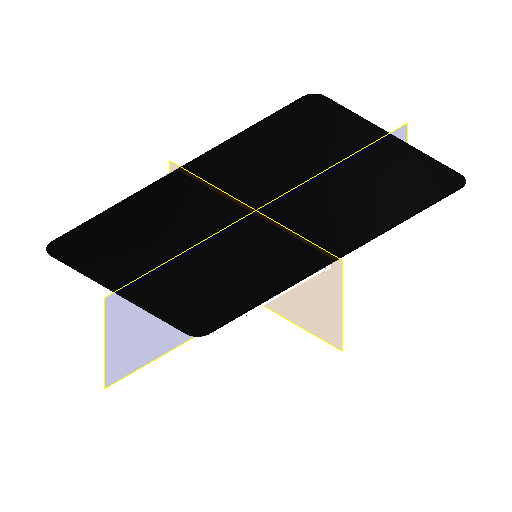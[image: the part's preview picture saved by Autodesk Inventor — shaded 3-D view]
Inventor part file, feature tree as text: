
AUTODESK INVENTOR PART (.ipt)
format: ipt  version: 2025.1 (Build 291241020, 241B)  size: 7,592,448 bytes
history: native  units: mm
features: other x246, plane x2
ambient origin geometry x8: Origin, YZ Plane, XZ Plane, XY Plane, X Axis, Y Axis, Z Axis, Center Point
bodies: Volumenkörper1 (feature_tree), Volumenkörper2 (feature_tree), Volumenkörper3 (feature_tree), Volumenkörper4 (feature_tree), Volumenkörper5 (feature_tree), Volumenkörper6 (feature_tree), Volumenkörper7 (feature_tree), Volumenkörper8 (feature_tree), Volumenkörper9 (feature_tree), Volumenkörper10 (feature_tree), Volumenkörper11 (feature_tree), Volumenkörper12 (feature_tree), Volumenkörper13 (feature_tree), Volumenkörper14 (feature_tree), Volumenkörper15 (feature_tree), Volumenkörper16 (feature_tree), Volumenkörper17 (feature_tree), Volumenkörper18 (feature_tree), Volumenkörper19 (feature_tree), Volumenkörper20 (feature_tree), Volumenkörper21 (feature_tree), Volumenkörper22 (feature_tree), Volumenkörper23 (feature_tree), Volumenkörper24 (feature_tree), Volumenkörper25 (feature_tree), Volumenkörper26 (feature_tree), Volumenkörper27 (feature_tree), Volumenkörper28 (feature_tree), Volumenkörper29 (feature_tree), Volumenkörper30 (feature_tree), Volumenkörper31 (feature_tree), Volumenkörper32 (feature_tree), Volumenkörper33 (feature_tree), Volumenkörper34 (feature_tree), Volumenkörper35 (feature_tree), Volumenkörper36 (feature_tree), Volumenkörper37 (feature_tree), Volumenkörper38 (feature_tree), Volumenkörper39 (feature_tree), Volumenkörper40 (feature_tree), Volumenkörper41 (feature_tree), Volumenkörper42 (feature_tree), Volumenkörper43 (feature_tree), Volumenkörper44 (feature_tree), Volumenkörper45 (feature_tree), Volumenkörper46 (feature_tree), Volumenkörper47 (feature_tree), Volumenkörper48 (feature_tree), Volumenkörper49 (feature_tree), Volumenkörper50 (feature_tree), Volumenkörper51 (feature_tree), Volumenkörper52 (feature_tree), Volumenkörper53 (feature_tree), Volumenkörper54 (feature_tree), Volumenkörper55 (feature_tree), Volumenkörper56 (feature_tree), Volumenkörper57 (feature_tree), Volumenkörper58 (feature_tree), Volumenkörper59 (feature_tree), Volumenkörper60 (feature_tree), Volumenkörper61 (feature_tree), Volumenkörper62 (feature_tree), Volumenkörper63 (feature_tree), Volumenkörper64 (feature_tree), Volumenkörper65 (feature_tree), Volumenkörper66 (feature_tree), Volumenkörper67 (feature_tree), Volumenkörper68 (feature_tree), Volumenkörper69 (feature_tree), Volumenkörper70 (feature_tree), Volumenkörper71 (feature_tree), Volumenkörper72 (feature_tree), Volumenkörper73 (feature_tree), Volumenkörper74 (feature_tree), Volumenkörper75 (feature_tree), Volumenkörper76 (feature_tree), Volumenkörper77 (feature_tree), Volumenkörper78 (feature_tree), Volumenkörper79 (feature_tree), Volumenkörper80 (feature_tree), Volumenkörper81 (feature_tree), Volumenkörper82 (feature_tree), Volumenkörper83 (feature_tree), Volumenkörper84 (feature_tree), Volumenkörper85 (feature_tree), Volumenkörper86 (feature_tree), Volumenkörper87 (feature_tree), Volumenkörper88 (feature_tree), Volumenkörper89 (feature_tree), Volumenkörper90 (feature_tree), Volumenkörper91 (feature_tree), Volumenkörper92 (feature_tree), Volumenkörper93 (feature_tree), Volumenkörper94 (feature_tree), Volumenkörper95 (feature_tree), Volumenkörper96 (feature_tree), Volumenkörper97 (feature_tree), Volumenkörper98 (feature_tree), Volumenkörper99 (feature_tree), Volumenkörper100 (feature_tree), Volumenkörper101 (feature_tree), Volumenkörper102 (feature_tree), Volumenkörper103 (feature_tree), Volumenkörper104 (feature_tree), Volumenkörper105 (feature_tree), Volumenkörper106 (feature_tree), Volumenkörper107 (feature_tree), Volumenkörper108 (feature_tree), Volumenkörper109 (feature_tree), Volumenkörper110 (feature_tree), Volumenkörper111 (feature_tree), Volumenkörper112 (feature_tree), Volumenkörper113 (feature_tree), Volumenkörper114 (feature_tree), Volumenkörper115 (feature_tree), Volumenkörper116 (feature_tree), Volumenkörper117 (feature_tree), Volumenkörper118 (feature_tree), Volumenkörper119 (feature_tree), Volumenkörper120 (feature_tree), Volumenkörper121 (feature_tree), Volumenkörper122 (feature_tree), Volumenkörper123 (feature_tree), Volumenkörper124 (feature_tree), Volumenkörper125 (feature_tree), Volumenkörper126 (feature_tree), Volumenkörper127 (feature_tree), Volumenkörper128 (feature_tree), Volumenkörper129 (feature_tree), Volumenkörper130 (feature_tree), Volumenkörper131 (feature_tree), Volumenkörper132 (feature_tree), Volumenkörper133 (feature_tree), Volumenkörper134 (feature_tree), Volumenkörper135 (feature_tree), Volumenkörper136 (feature_tree), Volumenkörper137 (feature_tree), Volumenkörper138 (feature_tree), Volumenkörper139 (feature_tree), Volumenkörper140 (feature_tree), Volumenkörper141 (feature_tree), Volumenkörper142 (feature_tree), Volumenkörper143 (feature_tree), Volumenkörper144 (feature_tree), Volumenkörper145 (feature_tree), Volumenkörper146 (feature_tree), Volumenkörper147 (feature_tree), Volumenkörper148 (feature_tree), Volumenkörper149 (feature_tree), Volumenkörper150 (feature_tree), Volumenkörper151 (feature_tree), Volumenkörper152 (feature_tree), Volumenkörper153 (feature_tree), Volumenkörper154 (feature_tree), Volumenkörper155 (feature_tree), Volumenkörper156 (feature_tree), Volumenkörper157 (feature_tree), Volumenkörper158 (feature_tree), Volumenkörper159 (feature_tree), Volumenkörper160 (feature_tree), Volumenkörper161 (feature_tree), Volumenkörper162 (feature_tree), Volumenkörper163 (feature_tree), Volumenkörper164 (feature_tree), Volumenkörper165 (feature_tree), Volumenkörper166 (feature_tree), Volumenkörper167 (feature_tree), Volumenkörper168 (feature_tree), Volumenkörper169 (feature_tree), Volumenkörper170 (feature_tree), Volumenkörper171 (feature_tree), Volumenkörper172 (feature_tree), Volumenkörper173 (feature_tree), Volumenkörper174 (feature_tree), Volumenkörper175 (feature_tree), Volumenkörper176 (feature_tree), Volumenkörper177 (feature_tree), Volumenkörper178 (feature_tree), Volumenkörper179 (feature_tree), Volumenkörper180 (feature_tree), Volumenkörper181 (feature_tree), Volumenkörper182 (feature_tree), Volumenkörper183 (feature_tree), Volumenkörper184 (feature_tree), Volumenkörper185 (feature_tree), Volumenkörper186 (feature_tree), Volumenkörper187 (feature_tree), Volumenkörper188 (feature_tree), Volumenkörper189 (feature_tree), Volumenkörper190 (feature_tree), Volumenkörper191 (feature_tree), Volumenkörper192 (feature_tree), Volumenkörper193 (feature_tree), Volumenkörper194 (feature_tree), Volumenkörper195 (feature_tree), Volumenkörper196 (feature_tree), Volumenkörper197 (feature_tree), Volumenkörper198 (feature_tree), Volumenkörper199 (feature_tree), Volumenkörper200 (feature_tree), Volumenkörper201 (feature_tree), Volumenkörper202 (feature_tree), Volumenkörper203 (feature_tree), Volumenkörper204 (feature_tree), Volumenkörper205 (feature_tree), Volumenkörper206 (feature_tree), Volumenkörper207 (feature_tree), Volumenkörper208 (feature_tree), Volumenkörper209 (feature_tree), Volumenkörper210 (feature_tree), Volumenkörper211 (feature_tree), Volumenkörper212 (feature_tree), Volumenkörper213 (feature_tree), Volumenkörper214 (feature_tree), Volumenkörper215 (feature_tree), Volumenkörper216 (feature_tree), Volumenkörper217 (feature_tree), Volumenkörper218 (feature_tree), Volumenkörper219 (feature_tree), Volumenkörper220 (feature_tree), Volumenkörper221 (feature_tree), Volumenkörper222 (feature_tree), Volumenkörper223 (feature_tree), Volumenkörper224 (feature_tree), Volumenkörper225 (feature_tree), Volumenkörper226 (feature_tree), Volumenkörper227 (feature_tree), Volumenkörper228 (feature_tree), Volumenkörper229 (feature_tree), Volumenkörper230 (feature_tree), Volumenkörper231 (feature_tree), Volumenkörper232 (feature_tree), Volumenkörper233 (feature_tree), Volumenkörper234 (feature_tree), Volumenkörper235 (feature_tree), Volumenkörper236 (feature_tree), Volumenkörper237 (feature_tree), Volumenkörper238 (feature_tree), Volumenkörper239 (feature_tree), Volumenkörper240 (feature_tree), Volumenkörper241 (feature_tree), Volumenkörper242 (feature_tree), Volumenkörper243 (feature_tree), Volumenkörper244 (feature_tree), Volumenkörper245 (feature_tree), Volumenkörper246 (feature_tree)
feature tree (248):
  plane  "Arbeitsebene1"
  plane  "Arbeitsebene2"
  other  "raspberry pi display_1:1"
  other  "raspberry pi display_1:2"
  other  "raspberry pi display_1:3"
  other  "Raspberry Pi 3 _1:1"
  other  "Raspberry Pi 3 _1:2"
  other  "Raspberry Pi 3 _1:3"
  other  "Raspberry Pi 3 _1:4"
  other  "Raspberry Pi 3 _1:5"
  other  "Raspberry Pi 3 _1:6"
  other  "Raspberry Pi 3 _1:7"
  other  "Raspberry Pi 3 _1:8"
  other  "Raspberry Pi 3 _1:9"
  other  "Raspberry Pi 3 _1:10"
  other  "Raspberry Pi 3 _1:11"
  other  "Raspberry Pi 3 _1:12"
  other  "Raspberry Pi 3 _1:13"
  other  "Raspberry Pi 3 _1:14"
  other  "Raspberry Pi 3 _1:15"
  other  "Raspberry Pi 3 _1:16"
  other  "Raspberry Pi 3 _1:17"
  other  "Raspberry Pi 3 _1:18"
  other  "Raspberry Pi 3 _1:19"
  other  "Raspberry Pi 3 _1:20"
  other  "Raspberry Pi 3 _1:21"
  other  "Raspberry Pi 3 _1:22"
  other  "Raspberry Pi 3 _1:23"
  other  "Raspberry Pi 3 _1:24"
  other  "Raspberry Pi 3 _1:25"
  other  "Raspberry Pi 3 _1:26"
  other  "Raspberry Pi 3 _1:27"
  other  "Raspberry Pi 3 _1:28"
  other  "Raspberry Pi 3 _1:29"
  other  "Raspberry Pi 3 _1:30"
  other  "Raspberry Pi 3 _1:31"
  other  "Raspberry Pi 3 _1:32"
  other  "Raspberry Pi 3 _1:33"
  other  "Raspberry Pi 3 _1:34"
  other  "Raspberry Pi 3 _1:35"
  other  "Raspberry Pi 3 _1:36"
  other  "Raspberry Pi 3 _1:37"
  other  "Raspberry Pi 3 _1:38"
  other  "Raspberry Pi 3 _1:39"
  other  "Raspberry Pi 3 _1:40"
  other  "Raspberry Pi 3 _1:41"
  other  "Raspberry Pi 3 _1:42"
  other  "Raspberry Pi 3 _1:43"
  other  "Raspberry Pi 3 _1:44"
  other  "Raspberry Pi 3 _1:45"
  other  "Raspberry Pi 3 _1:46"
  other  "Raspberry Pi 3 _1:47"
  other  "Raspberry Pi 3 _1:48"
  other  "Raspberry Pi 3 _1:49"
  other  "Raspberry Pi 3 _1:50"
  other  "Raspberry Pi 3 _1:51"
  other  "Raspberry Pi 3 _1:52"
  other  "Raspberry Pi 3 _1:53"
  other  "Raspberry Pi 3 _1:54"
  other  "Raspberry Pi 3 _1:55"
  other  "Raspberry Pi 3 _1:56"
  other  "Raspberry Pi 3 _1:57"
  other  "Raspberry Pi 3 _1:58"
  other  "Raspberry Pi 3 _1:59"
  other  "Raspberry Pi 3 _1:60"
  other  "Raspberry Pi 3 _1:61"
  other  "Raspberry Pi 3 _1:62"
  other  "Raspberry Pi 3 _1:63"
  other  "Raspberry Pi 3 _1:64"
  other  "Raspberry Pi 3 _1:65"
  other  "Raspberry Pi 3 _1:66"
  other  "Raspberry Pi 3 _1:67"
  other  "Raspberry Pi 3 _1:68"
  other  "Raspberry Pi 3 _1:69"
  other  "Raspberry Pi 3 _1:70"
  other  "Raspberry Pi 3 _1:71"
  other  "Raspberry Pi 3 _1:72"
  other  "Raspberry Pi 3 _1:73"
  other  "Raspberry Pi 3 _1:74"
  other  "Raspberry Pi 3 _1:75"
  other  "Raspberry Pi 3 _1:76"
  other  "Raspberry Pi 3 _1:77"
  other  "Raspberry Pi 3 _1:78"
  other  "Raspberry Pi 3 _1:79"
  other  "Raspberry Pi 3 _1:80"
  other  "Raspberry Pi 3 _1:81"
  other  "Raspberry Pi 3 _1:82"
  other  "Raspberry Pi 3 _1:83"
  other  "Raspberry Pi 3 _1:84"
  other  "Raspberry Pi 3 _1:85"
  other  "Raspberry Pi 3 _1:86"
  other  "Raspberry Pi 3 _1:87"
  other  "Raspberry Pi 3 _1:88"
  other  "Raspberry Pi 3 _1:89"
  other  "Raspberry Pi 3 _1:90"
  other  "Raspberry Pi 3 _1:91"
  other  "Raspberry Pi 3 _1:92"
  other  "Raspberry Pi 3 _1:93"
  other  "Raspberry Pi 3 _1:94"
  other  "Raspberry Pi 3 _1:95"
  other  "Raspberry Pi 3 _1:96"
  other  "Raspberry Pi 3 _1:97"
  other  "Raspberry Pi 3 _1:98"
  other  "Raspberry Pi 3 _1:99"
  other  "Raspberry Pi 3 _1:100"
  other  "Raspberry Pi 3 _1:101"
  other  "Raspberry Pi 3 _1:102"
  other  "Raspberry Pi 3 _1:103"
  other  "Raspberry Pi 3 _1:104"
  other  "Raspberry Pi 3 _1:105"
  other  "Raspberry Pi 3 _1:106"
  other  "Raspberry Pi 3 _1:107"
  other  "Raspberry Pi 3 _1:108"
  other  "Raspberry Pi 3 _1:109"
  other  "Raspberry Pi 3 _1:110"
  other  "Raspberry Pi 3 _1:111"
  other  "Raspberry Pi 3 _1:112"
  other  "Raspberry Pi 3 _1:113"
  other  "Raspberry Pi 3 _1:114"
  other  "Raspberry Pi 3 _1:115"
  other  "Raspberry Pi 3 _1:116"
  other  "Raspberry Pi 3 _1:117"
  other  "Raspberry Pi 3 _1:118"
  other  "Raspberry Pi 3 _1:119"
  other  "Raspberry Pi 3 _1:120"
  other  "Raspberry Pi 3 _1:121"
  other  "Raspberry Pi 3 _1:122"
  other  "Raspberry Pi 3 _1:123"
  other  "Raspberry Pi 3 _1:124"
  other  "Raspberry Pi 3 _1:125"
  other  "Raspberry Pi 3 _1:126"
  other  "Raspberry Pi 3 _1:127"
  other  "Raspberry Pi 3 _1:128"
  other  "Raspberry Pi 3 _1:129"
  other  "Raspberry Pi 3 _1:130"
  other  "Raspberry Pi 3 _1:131"
  other  "Raspberry Pi 3 _1:132"
  other  "Raspberry Pi 3 _1:133"
  other  "Raspberry Pi 3 _1:134"
  other  "Raspberry Pi 3 _1:135"
  other  "Raspberry Pi 3 _1:136"
  other  "Raspberry Pi 3 _1:137"
  other  "Raspberry Pi 3 _1:138"
  other  "Raspberry Pi 3 _1:139"
  other  "Raspberry Pi 3 _1:140"
  other  "Raspberry Pi 3 _1:141"
  other  "Raspberry Pi 3 _1:142"
  other  "Raspberry Pi 3 _1:143"
  other  "Raspberry Pi 3 _1:144"
  other  "Raspberry Pi 3 _1:145"
  other  "Raspberry Pi 3 _1:146"
  other  "Raspberry Pi 3 _1:147"
  other  "Raspberry Pi 3 _1:148"
  other  "Raspberry Pi 3 _1:149"
  other  "Raspberry Pi 3 _1:150"
  other  "Raspberry Pi 3 _1:151"
  other  "Raspberry Pi 3 _1:152"
  other  "Raspberry Pi 3 _1:153"
  other  "Raspberry Pi 3 _1:154"
  other  "Raspberry Pi 3 _1:155"
  other  "Raspberry Pi 3 _1:156"
  other  "Raspberry Pi 3 _1:157"
  other  "Raspberry Pi 3 _1:158"
  other  "Raspberry Pi 3 _1:159"
  other  "Raspberry Pi 3 _1:160"
  other  "Raspberry Pi 3 _1:161"
  other  "Raspberry Pi 3 _1:162"
  other  "Raspberry Pi 3 _1:163"
  other  "Raspberry Pi 3 _1:164"
  other  "Raspberry Pi 3 _1:165"
  other  "Raspberry Pi 3 _1:166"
  other  "Raspberry Pi 3 _1:167"
  other  "Raspberry Pi 3 _1:168"
  other  "Raspberry Pi 3 _1:169"
  other  "Raspberry Pi 3 _1:170"
  other  "Raspberry Pi 3 _1:171"
  other  "Raspberry Pi 3 _1:172"
  other  "Raspberry Pi 3 _1:173"
  other  "Raspberry Pi 3 _1:174"
  other  "Raspberry Pi 3 _1:175"
  other  "Raspberry Pi 3 _1:176"
  other  "Raspberry Pi 3 _1:177"
  other  "Raspberry Pi 3 _1:178"
  other  "Raspberry Pi 3 _1:179"
  other  "Raspberry Pi 3 _1:180"
  other  "Raspberry Pi 3 _1:181"
  other  "Raspberry Pi 3 _1:182"
  other  "Raspberry Pi 3 _1:183"
  other  "Raspberry Pi 3 _1:184"
  other  "Raspberry Pi 3 _1:185"
  other  "Raspberry Pi 3 _1:186"
  other  "Raspberry Pi 3 _1:187"
  other  "Raspberry Pi 3 _1:188"
  other  "Raspberry Pi 3 _1:189"
  other  "Raspberry Pi 3 _1:190"
  other  "Raspberry Pi 3 _1:191"
  other  "Raspberry Pi 3 _1:192"
  other  "Raspberry Pi 3 _1:193"
  other  "Raspberry Pi 3 _1:194"
  other  "Raspberry Pi 3 _1:195"
  other  "Raspberry Pi 3 _1:196"
  other  "Raspberry Pi 3 _1:197"
  other  "Raspberry Pi 3 _1:198"
  other  "Raspberry Pi 3 _1:199"
  other  "Raspberry Pi 3 _1:200"
  other  "Raspberry Pi 3 _1:201"
  other  "Raspberry Pi 3 _1:202"
  other  "Raspberry Pi 3 _1:203"
  other  "Raspberry Pi 3 _1:204"
  other  "Raspberry Pi 3 _1:205"
  other  "Raspberry Pi 3 _1:206"
  other  "Raspberry Pi 3 _1:207"
  other  "Raspberry Pi 3 _1:208"
  other  "Raspberry Pi 3 _1:209"
  other  "Raspberry Pi 3 _1:210"
  other  "Raspberry Pi 3 _1:211"
  other  "Raspberry Pi 3 _1:212"
  other  "Raspberry Pi 3 _1:213"
  other  "Raspberry Pi 3 _1:214"
  other  "Raspberry Pi 3 _1:215"
  other  "Raspberry Pi 3 _1:216"
  other  "Raspberry Pi 3 _1:217"
  other  "raspberry pi display module_1:1"
  other  "raspberry pi display module_1:2"
  other  "raspberry pi display module_1:3"
  other  "raspberry pi display module_1:4"
  other  "raspberry pi display module_1:5"
  other  "raspberry pi display module_1:6"
  other  "raspberry pi display module_1:7"
  other  "raspberry pi display module_1:8"
  other  "raspberry pi display module_1:9"
  other  "raspberry pi display module_1:10"
  other  "raspberry pi display module_1:11"
  other  "raspberry pi display module_1:12"
  other  "raspberry pi display module_1:13"
  other  "raspberry pi display module_1:14"
  other  "стойка 12мм_1:1"
  other  "стойка 12мм_2:1"
  other  "стойка 12мм_3:1"
  other  "стойка 12мм_4:1"
  other  "cables_1:1"
  other  "cables_1:2"
  other  "cables_1:3"
  other  "cables_1:4"
  other  "ISO 7045 H M2,5 x 3 - 4.8 - H_1:1"
  other  "ISO 7045 H M2,5 x 3 - 4.8 - H_2:1"
  other  "ISO 7045 H M2,5 x 3 - 4.8 - H_3:1"
  other  "ISO 7045 H M2,5 x 3 - 4.8 - H_4:1"
